# Revit family: Sensor-Lutron-Wall-LOS_W_Series-Occupancy-LOS-WDT-R-WH
name_source: partatom
category: Lighting Devices
units: mm (PartAtom-declared; Revit-internal decimal feet)

## family parameters
Cut with Voids When Loaded = No
Host = Face
Maintain Annotation Orientation = No
OmniClass Number = 23.85.80.11.27
OmniClass Title = Lighting Controls
Part Type = Normal
Room Calculation Point = No
Round Connector Dimension = Use Diameter
Shared = No

## types (1)
- LOS-WDT-R-WH
    Assembly Code = D5030800
    CP Pan = 0.00°
    CP Tilt = 0.00°
    Coverage = 1600 SF
    Coverage Area = 1600 sqft (148 m2)
    Default Elevation = 48 "
    Depth = 3.9 "
    Description = Wall-mounted occupancy and vacancy sensor
    Field of View = 110.00°
    Finish = Plastic - Lutron - White
    Instruction Sheet Link = https://assets.lutron.com
    Keynote = 16500
    Length = 5.25 "
    Major Motion Coverage Range = US Major Motion: 32 ft x 32 ft (9.8 m x 9.8 m) / IR Major Motion: 40 ft (12.2 m)
    Manufacturer = Lutron Electronics Co., Inc
    Manufacturer Fax Number = 610-282-1243
    Maximum Operating Temperature = 104 °F / 40 °C
    Minimum Operating Temperature = 32 °F / 0 °C
    Minor Motion Coverage Range = US Minor Motion: 23 ft x 23 ft (7.0 m x 7.0 m) / IR Minor Motion:  20 ft (6.1 m)
    Model = LOS-WDT-R-WH
    Number of Poles = 1
    Performance URL = https://www.lutron.com
    Power Factor = 1
    Product Documentation Link = https://assets.lutron.com
    Product Name = LOS-W series wall-mount occupancy sensor
    Product Page URL = https://www.lutron.com
    Sensor Type = Occupancy Dual Technology
    Series = LOS-W Series
    URL = http://www.lutron.com
    Version = 2021 - v1.0a
    Video Link = https://www.youtube.com
    Voltage = 20 V
    Voltage Comment = Operating voltage: 20 – 24 V
    Warranty URL = https://www.lutron.com
    Width = 2.7 "

## geometry (parser evidence)
native form markers: Sweep x7
no freeform markers — native parametric forms only
